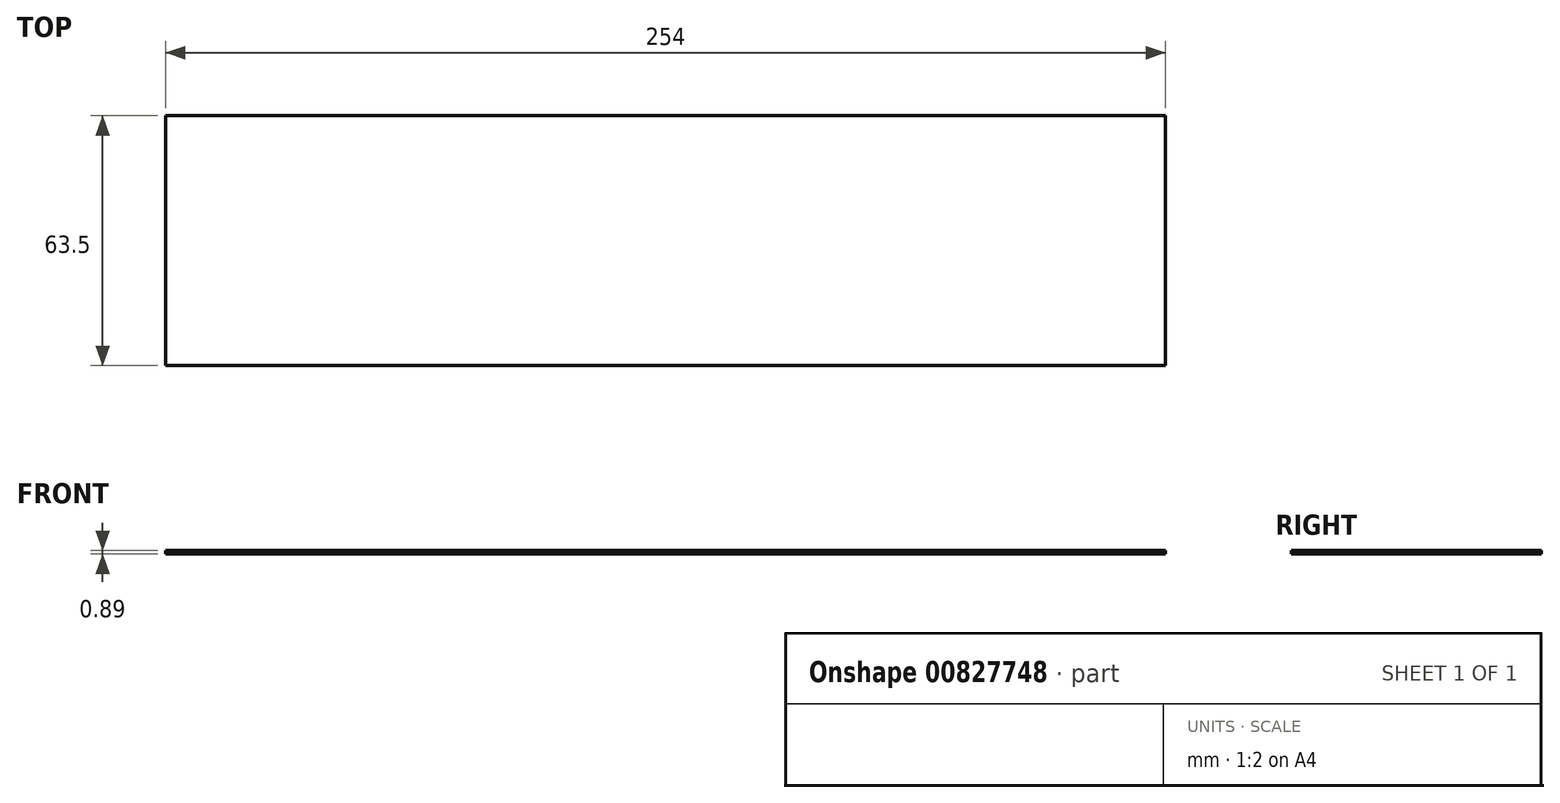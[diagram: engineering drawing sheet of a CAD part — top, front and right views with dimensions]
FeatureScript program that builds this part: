
annotation { "Feature Type Name" : "Feature", "Feature Type Description" : "" }
export const myFeature = defineFeature(function(context is Context, id is Id, definition is map)
    precondition{}
    {
        {
            var Q0;
            Q0=qCreatedBy(makeId("Top.planeOp"),FACE);
            var sketch = newSketch(context, id + "F0", { "sketchPlane" : qUnion([Q0])});
            skLineSegment(sketch, "E0.bottom", {"start": v(-127, 31.75) * mm, "end": v(127, 31.75) * mm});
            skLineSegment(sketch, "E0.top", {"start": v(-127, -31.75) * mm, "end": v(127, -31.75) * mm});
            skLineSegment(sketch, "E0.left", {"start": v(-127, 31.75) * mm, "end": v(-127, -31.75) * mm});
            skLineSegment(sketch, "E0.right", {"start": v(127, 31.75) * mm, "end": v(127, -31.75) * mm});
            skSolve(sketch);
        }
        {
            var Q0;
            Q0=makeQuery(id+"F0.imprint","IMPRINT",FACE,{"disambiguationData":[TD([[makeQuery(id+"F0.imprint","IMPRINT",EDGE,{"derivedFrom":sQuery(id+"F0.wireOp",EDGE,"E0.bottom")}),-1.0]])]});
            extrude(context, id + "F1", {"entities" : qUnion([Q0]), "depth" : 0.89 * mm, "offsetDistance" : 25.4 * mm});
        }
    });
